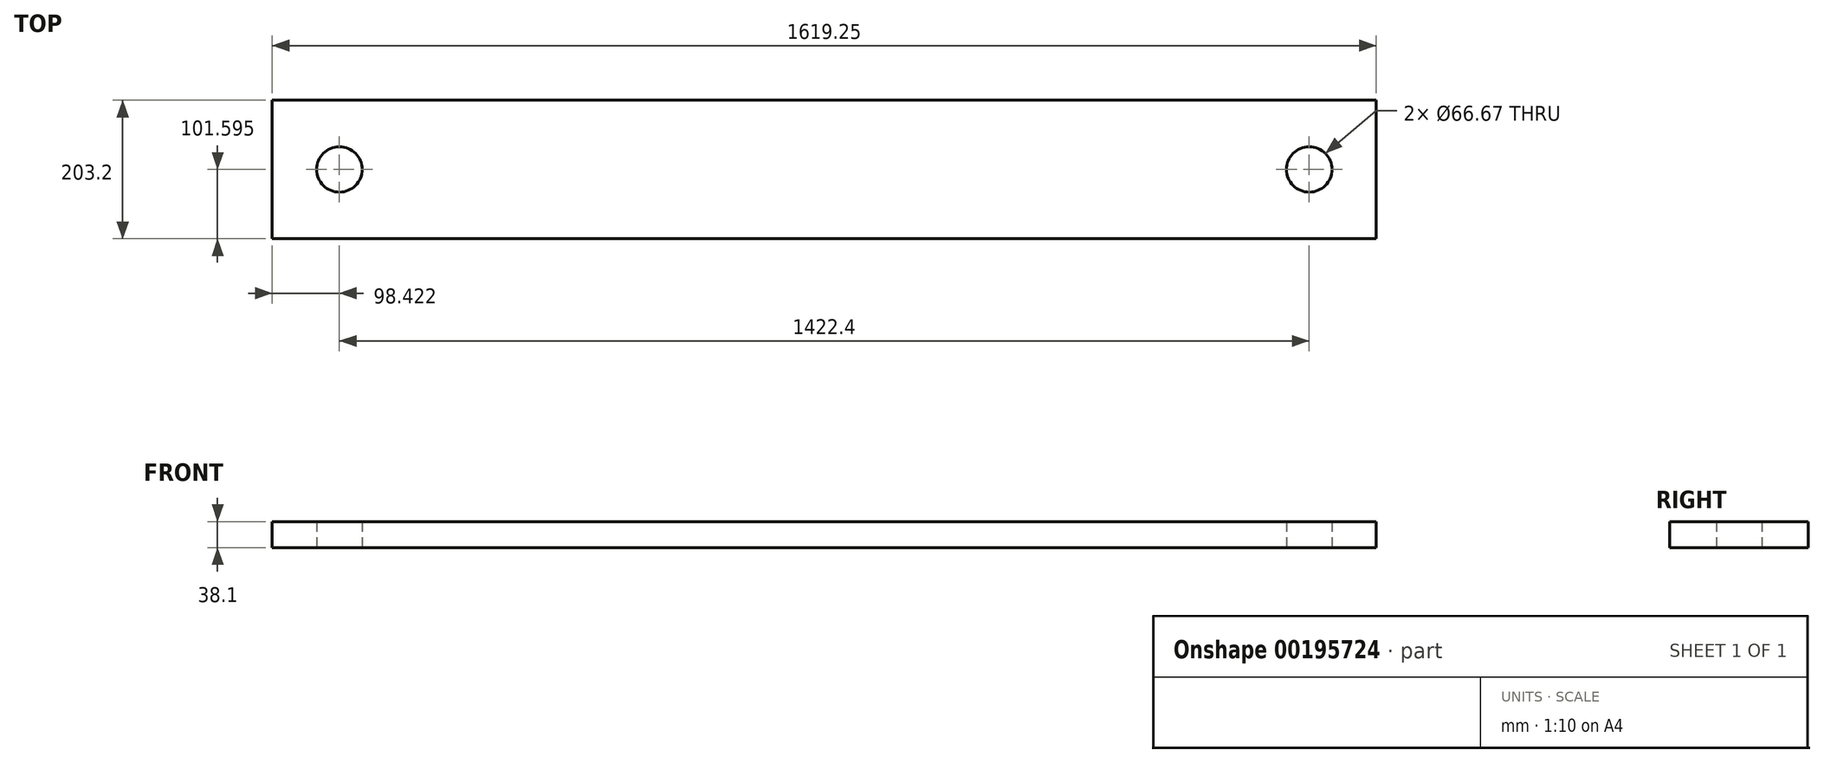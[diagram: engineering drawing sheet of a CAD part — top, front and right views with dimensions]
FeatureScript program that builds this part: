
annotation { "Feature Type Name" : "Feature", "Feature Type Description" : "" }
export const myFeature = defineFeature(function(context is Context, id is Id, definition is map)
    precondition{}
    {
        {
            var Q0;
            Q0=qCreatedBy(makeId("Top.planeOp"),FACE);
            var sketch = newSketch(context, id + "F0", { "sketchPlane" : qUnion([Q0])});
            skLineSegment(sketch, "E0.bottom", {"start": v(-795.96, -200.76) * mm, "end": v(823.29, -200.76) * mm});
            skLineSegment(sketch, "E0.top", {"start": v(-795.96, 2.44) * mm, "end": v(823.29, 2.44) * mm});
            skLineSegment(sketch, "E0.left", {"start": v(-795.96, -200.76) * mm, "end": v(-795.96, 2.44) * mm});
            skLineSegment(sketch, "E0.right", {"start": v(823.29, -200.76) * mm, "end": v(823.29, 2.44) * mm});
            skCircle(sketch, "E1", {"center": v(-697.54, -99.16) * mm, "radius": 33.34 * mm});
            skCircle(sketch, "E2", {"center": v(724.86, -99.16) * mm, "radius": 33.34 * mm});
            skSolve(sketch);
        }
        {
            var Q0;
            Q0=makeQuery(id+"F0.imprint","IMPRINT",FACE,{"disambiguationData":[TD([[makeQuery(id+"F0.imprint","IMPRINT",EDGE,{"derivedFrom":sQuery(id+"F0.wireOp",EDGE,"E0.bottom")}),1.0]])]});
            extrude(context, id + "F1", {"entities" : qUnion([Q0]), "depth" : 38.1 * mm});
        }
    });
